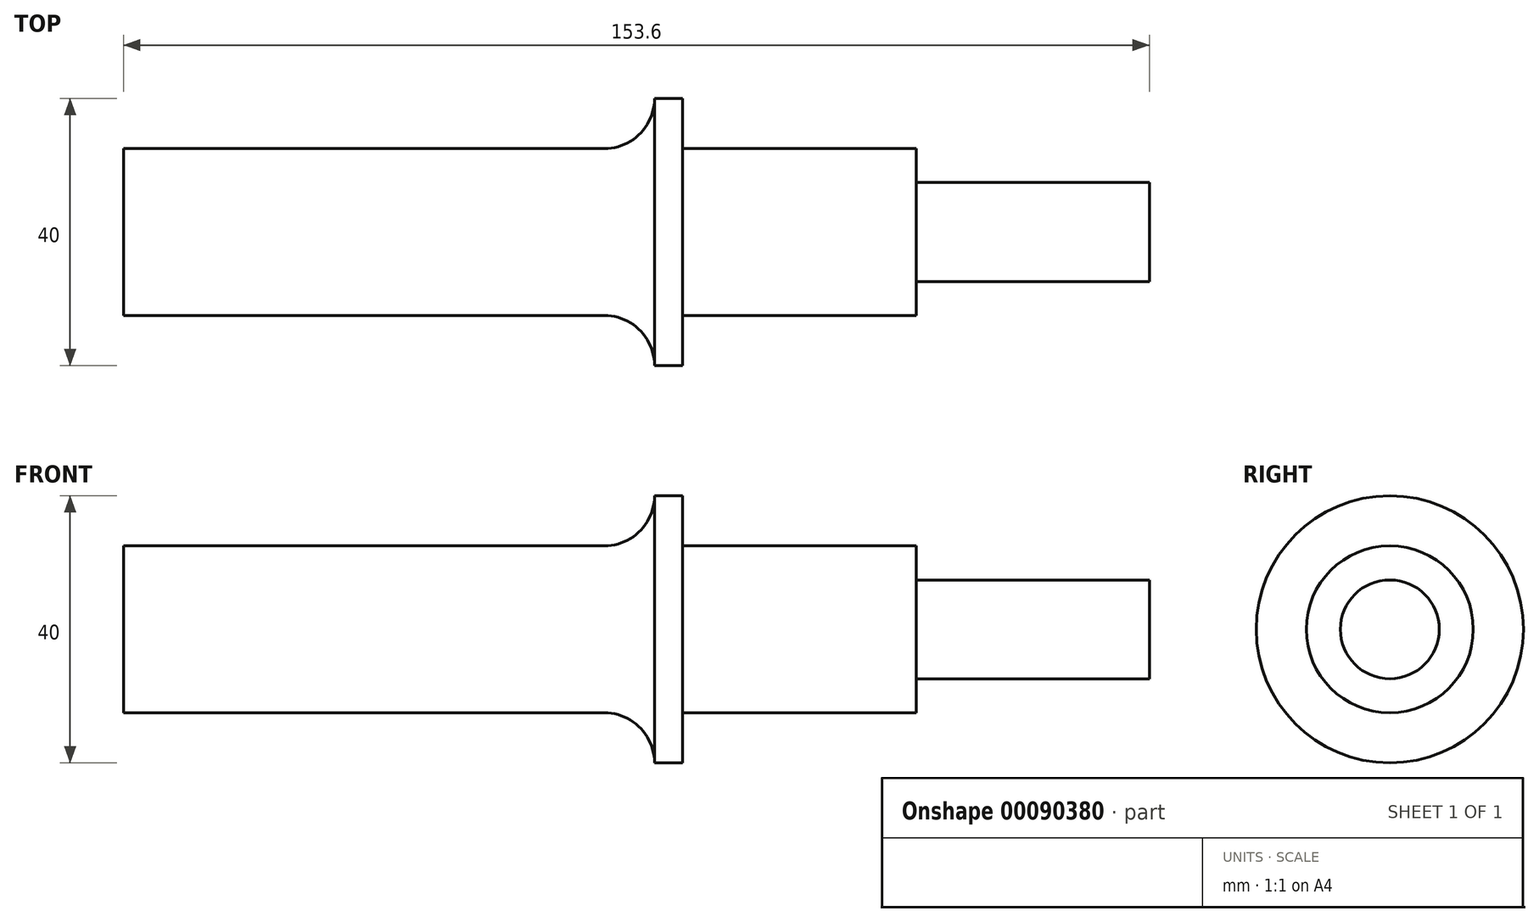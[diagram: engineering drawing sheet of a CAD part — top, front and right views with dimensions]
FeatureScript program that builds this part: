
annotation { "Feature Type Name" : "Feature", "Feature Type Description" : "" }
export const myFeature = defineFeature(function(context is Context, id is Id, definition is map)
    precondition{}
    {
        {
            var Q0;
            Q0=qCreatedBy(makeId("Front.planeOp"),FACE);
            var sketch = newSketch(context, id + "F0", { "sketchPlane" : qUnion([Q0])});
            skArc(sketch, "E0", {"start": v(14.93, -7.5) * mm, "mid": v(12.73, -2.2) * mm, "end": v(7.43, 0) * mm});
            skLineSegment(sketch, "E1", {"start": v(14.93, -7.5) * mm, "end": v(19.13, -7.5) * mm});
            skLineSegment(sketch, "E2", {"start": v(19.13, 0) * mm, "end": v(54.13, 0) * mm});
            skLineSegment(sketch, "E3", {"start": v(54.13, 5.1) * mm, "end": v(89.03, 5.1) * mm});
            skLineSegment(sketch, "E4", {"start": v(-64.57, 0) * mm, "end": v(7.43, 0) * mm});
            skLineSegment(sketch, "E5", {"start": v(-64.57, 12.5) * mm, "end": v(89.03, 12.5) * mm});
            skLineSegment(sketch, "E6", {"start": v(7.43, 0) * mm, "end": v(19.13, 0) * mm});
            skLineSegment(sketch, "E7", {"start": v(-64.57, 0) * mm, "end": v(-64.57, 12.5) * mm});
            skLineSegment(sketch, "E8", {"start": v(89.03, 5.1) * mm, "end": v(89.03, 12.5) * mm});
            skLineSegment(sketch, "E9", {"start": v(54.13, 0) * mm, "end": v(54.13, 5.1) * mm});
            skLineSegment(sketch, "E10.MirrorCS", {"start": v(54.13, 25) * mm, "end": v(54.13, 19.9) * mm});
            skLineSegment(sketch, "E11.MirrorCS", {"start": v(89.03, 19.9) * mm, "end": v(89.03, 12.5) * mm});
            skLineSegment(sketch, "E12.MirrorCS", {"start": v(-64.57, 25) * mm, "end": v(-64.57, 12.5) * mm});
            skLineSegment(sketch, "E13.MirrorCS", {"start": v(7.43, 25) * mm, "end": v(19.13, 25) * mm});
            skLineSegment(sketch, "E14.MirrorCS", {"start": v(-64.57, 25) * mm, "end": v(7.43, 25) * mm});
            skLineSegment(sketch, "E15.MirrorCS", {"start": v(54.13, 19.9) * mm, "end": v(89.03, 19.9) * mm});
            skLineSegment(sketch, "E16.MirrorCS", {"start": v(19.13, 25) * mm, "end": v(54.13, 25) * mm});
            skLineSegment(sketch, "E17.MirrorCS", {"start": v(14.93, 32.5) * mm, "end": v(19.13, 32.5) * mm});
            skArc(sketch, "E18.MirrorCS", {"start": v(14.93, 32.5) * mm, "mid": v(12.73, 27.2) * mm, "end": v(7.43, 25) * mm});
            skLineSegment(sketch, "E19", {"start": v(19.13, 32.5) * mm, "end": v(19.13, -7.5) * mm});
            skSolve(sketch);
        }
        {
            var Q0;
            Q0=makeQuery(id+"F0.imprint","IMPRINT",FACE,{"disambiguationData":[TD([[makeQuery(id+"F0.imprint","IMPRINT",EDGE,{"derivedFrom":sQuery(id+"F0.wireOp",EDGE,"E4")}),1.0]])]});
            var Q1;
            Q1=makeQuery(id+"F0.imprint","IMPRINT",FACE,{"disambiguationData":[TD([[makeQuery(id+"F0.imprint","IMPRINT",EDGE,{"derivedFrom":sQuery(id+"F0.wireOp",EDGE,"E0")}),-1.0]])]});
            var Q2;
            {var subQ1=sQuery(id+"F0.wireOp",EDGE,"E2");Q2=makeQuery(id+"F0.imprint","IMPRINT",FACE,{"disambiguationData":[TD([[makeQuery(id+"F0.imprint","IMPRINT",EDGE,{"derivedFrom":subQ1}),1.0]])]});}
            var Q3;
            Q3=sQuery(id+"F0.wireOp",EDGE,"E5");
            revolve(context, id + "F1", {"entities" : qUnion([Q0, Q1, Q2]), "axis" : qUnion([Q3]), "revolveType" : RevolveType.FULL});
        }
    });
